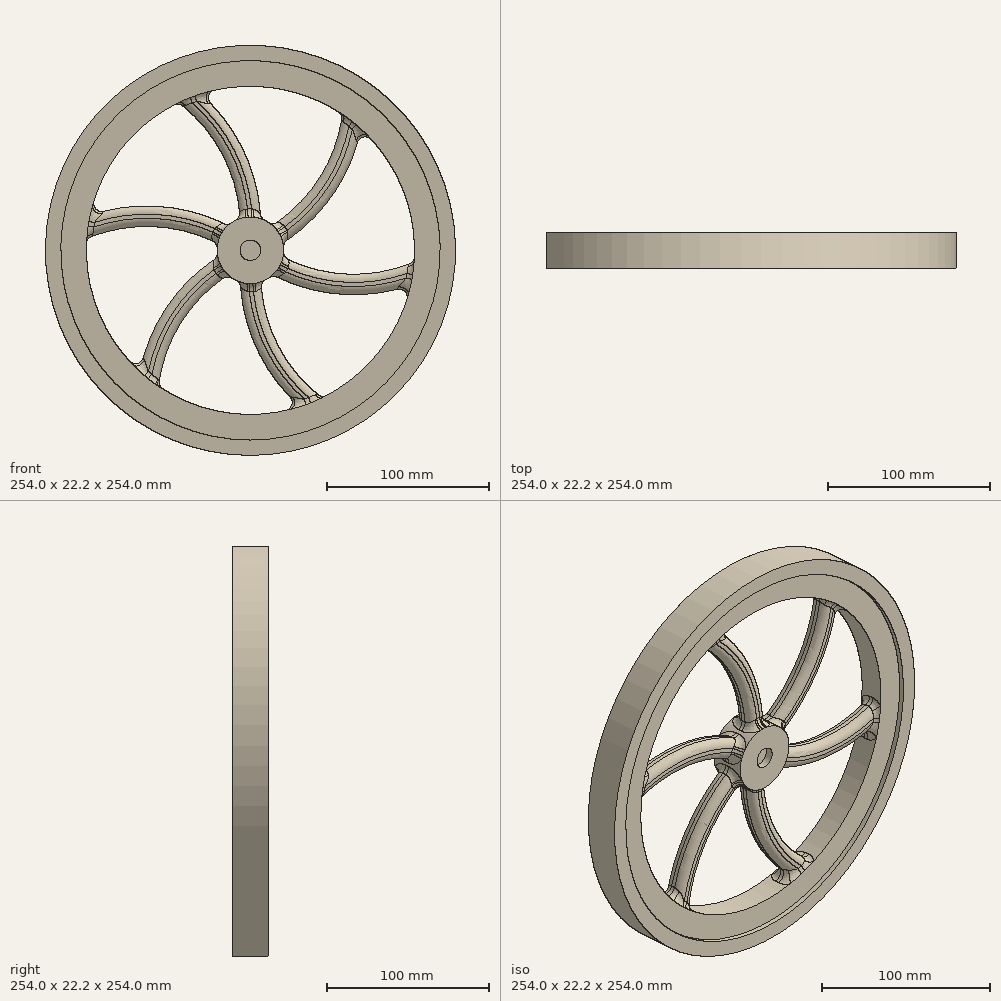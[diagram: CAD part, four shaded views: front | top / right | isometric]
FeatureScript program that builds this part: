
annotation { "Feature Type Name" : "Feature", "Feature Type Description" : "" }
export const myFeature = defineFeature(function(context is Context, id is Id, definition is map)
    precondition{}
    {
        {
            var Q0;
            Q0=qCreatedBy(makeId("Front.planeOp"),FACE);
            var sketch = newSketch(context, id + "F0", { "sketchPlane" : qUnion([Q0])});
            skCircle(sketch, "E0", {"center": v(0, 0) * mm, "radius": 127 * mm});
            skCircle(sketch, "E1", {"center": v(0, 0) * mm, "radius": 6.35 * mm});
            skCircle(sketch, "E2", {"center": v(0, 0) * mm, "radius": 101.6 * mm});
            skCircle(sketch, "E3", {"center": v(0, 0) * mm, "radius": 117.48 * mm});
            skCircle(sketch, "E4", {"center": v(0, 0) * mm, "radius": 20.64 * mm});
            skSolve(sketch);
        }
        {
            var Q0;
            Q0=makeQuery(id+"F0.imprint","IMPRINT",FACE,{"disambiguationData":[TD([[makeQuery(id+"F0.imprint","IMPRINT",EDGE,{"derivedFrom":sQuery(id+"F0.wireOp",EDGE,"E0")}),1.0]])]});
            extrude(context, id + "F1", {"entities" : qUnion([Q0]), "endBound" : BoundingType.SYMMETRIC, "depth" : 22.22 * mm, "offsetDistance" : 25.4 * mm});
        }
        {
            var Q0;
            Q0=makeQuery(id+"F0.imprint","IMPRINT",FACE,{"disambiguationData":[TD([[makeQuery(id+"F0.imprint","IMPRINT",EDGE,{"derivedFrom":sQuery(id+"F0.wireOp",EDGE,"E2")}),-1.0]])]});
            extrude(context, id + "F2", {"entities" : qUnion([Q0]), "operationType" : NewBodyOperationType.ADD, "endBound" : BoundingType.SYMMETRIC, "depth" : 15.88 * mm, "offsetDistance" : 25.4 * mm});
        }
        {
            var Q0;
            Q0=makeQuery(id+"F0.imprint","IMPRINT",FACE,{"disambiguationData":[TD([[makeQuery(id+"F0.imprint","IMPRINT",EDGE,{"derivedFrom":sQuery(id+"F0.wireOp",EDGE,"E1")}),-1.0]])]});
            extrude(context, id + "F3", {"entities" : qUnion([Q0]), "endBound" : BoundingType.SYMMETRIC, "depth" : 22.22 * mm, "offsetDistance" : 25.4 * mm});
        }
        {
            var Q0;
            Q0=makeQuery(id+"F0.imprint","IMPRINT",FACE,{"disambiguationData":[TD([[makeQuery(id+"F0.imprint","IMPRINT",EDGE,{"derivedFrom":sQuery(id+"F0.wireOp",EDGE,"E2")}),1.0]])]});
            var sketch = newSketch(context, id + "F4", { "sketchPlane" : qUnion([Q0])});
            skLineSegment(sketch, "E5", {"start": v(0, 0) * mm, "end": v(0, 137.05) * mm, "construction": true});
            skArc(sketch, "E6", {"start": v(0, 14.86) * mm, "mid": v(-11.63, 62.26) * mm, "end": v(-43.88, 98.88) * mm});
            skArc(sketch, "E7.0.startCap", {"start": v(6.35, 14.86) * mm, "mid": v(0, 8.51) * mm, "end": v(-6.35, 14.86) * mm});
            skArc(sketch, "E7.0.endCap", {"start": v(-47.5, 93.67) * mm, "mid": v(-49.09, 102.51) * mm, "end": v(-40.25, 104.1) * mm});
            skArc(sketch, "E7.0.left", {"start": v(-6.35, 14.86) * mm, "mid": v(-17.26, 59.32) * mm, "end": v(-47.5, 93.67) * mm});
            skArc(sketch, "E7.0.right", {"start": v(6.35, 14.86) * mm, "mid": v(-6, 65.2) * mm, "end": v(-40.25, 104.1) * mm});
            skArc(sketch, "E8.1.0", {"start": v(-9.7, 12.93) * mm, "mid": v(-59.46, 27.4) * mm, "end": v(-110.27, 17.19) * mm});
            skArc(sketch, "E8.1.1", {"start": v(-104.88, 5.7) * mm, "mid": v(-113.32, 8.74) * mm, "end": v(-110.27, 17.19) * mm});
            skArc(sketch, "E8.1.2", {"start": v(-16.04, 1.93) * mm, "mid": v(-60, 14.71) * mm, "end": v(-104.88, 5.7) * mm});
            skArc(sketch, "E8.1.3", {"start": v(-9.7, 12.93) * mm, "mid": v(-7.37, 4.26) * mm, "end": v(-16.04, 1.93) * mm});
            skArc(sketch, "E8.2.0", {"start": v(-16.04, -1.93) * mm, "mid": v(-53.46, -37.8) * mm, "end": v(-70.02, -86.9) * mm});
            skArc(sketch, "E8.2.1", {"start": v(-57.37, -87.98) * mm, "mid": v(-64.23, -93.77) * mm, "end": v(-70.02, -86.9) * mm});
            skArc(sketch, "E8.2.2", {"start": v(-9.7, -12.93) * mm, "mid": v(-42.74, -44.6) * mm, "end": v(-57.37, -87.98) * mm});
            skArc(sketch, "E8.2.3", {"start": v(-16.04, -1.93) * mm, "mid": v(-7.37, -4.26) * mm, "end": v(-9.7, -12.93) * mm});
            skArc(sketch, "E8.3.0", {"start": v(-6.35, -14.86) * mm, "mid": v(6, -65.2) * mm, "end": v(40.25, -104.1) * mm});
            skArc(sketch, "E8.3.1", {"start": v(47.5, -93.67) * mm, "mid": v(49.09, -102.51) * mm, "end": v(40.25, -104.1) * mm});
            skArc(sketch, "E8.3.2", {"start": v(6.35, -14.86) * mm, "mid": v(17.26, -59.32) * mm, "end": v(47.5, -93.67) * mm});
            skArc(sketch, "E8.3.3", {"start": v(-6.35, -14.86) * mm, "mid": v(0, -8.51) * mm, "end": v(6.35, -14.86) * mm});
            skArc(sketch, "E8.4.0", {"start": v(9.7, -12.93) * mm, "mid": v(59.46, -27.4) * mm, "end": v(110.27, -17.19) * mm});
            skArc(sketch, "E8.4.1", {"start": v(104.88, -5.7) * mm, "mid": v(113.32, -8.74) * mm, "end": v(110.27, -17.19) * mm});
            skArc(sketch, "E8.4.2", {"start": v(16.04, -1.93) * mm, "mid": v(60, -14.71) * mm, "end": v(104.88, -5.7) * mm});
            skArc(sketch, "E8.4.3", {"start": v(9.7, -12.93) * mm, "mid": v(7.37, -4.26) * mm, "end": v(16.04, -1.93) * mm});
            skArc(sketch, "E8.5.0", {"start": v(16.04, 1.93) * mm, "mid": v(53.46, 37.8) * mm, "end": v(70.02, 86.9) * mm});
            skArc(sketch, "E8.5.1", {"start": v(57.37, 87.98) * mm, "mid": v(64.23, 93.77) * mm, "end": v(70.02, 86.9) * mm});
            skArc(sketch, "E8.5.2", {"start": v(9.7, 12.93) * mm, "mid": v(42.74, 44.6) * mm, "end": v(57.37, 87.98) * mm});
            skArc(sketch, "E8.5.3", {"start": v(16.04, 1.93) * mm, "mid": v(7.37, 4.26) * mm, "end": v(9.7, 12.93) * mm});
            skPoint(sketch, "E8.center", {"position": v(0, 0) * mm});
            skSolve(sketch);
        }
        {
            var Q0;
            {var subQ0=sQuery(id+"F4.wireOp",EDGE,"E6");var subQ1=makeQuery(id+"F0.imprint","IMPRINT",EDGE,{"derivedFrom":sQuery(id+"F0.wireOp",EDGE,"E2")});var subQ2=makeQuery(id+"F4.imprint","INTERSECT",VERTEX,{"derivedFrom":[subQ1,subQ0]});Q0=makeQuery(id+"F4.imprint","IMPRINT",FACE,{"disambiguationData":[TD([[makeQuery(id+"F4.imprint","IMPRINT",EDGE,{"disambiguationData":[TD([[subQ2,1.0]])],"derivedFrom":subQ0}),1.0]])]});}
            var Q1;
            {var subQ0=sQuery(id+"F4.wireOp",EDGE,"E8.3.1");Q1=makeQuery(id+"F4.imprint","IMPRINT",FACE,{"disambiguationData":[TD([[makeQuery(id+"F4.imprint","IMPRINT",EDGE,{"derivedFrom":subQ0}),-1.0]])]});}
            var Q2;
            {var subQ4=sQuery(id+"F4.wireOp",EDGE,"E7.0.startCap");Q2=makeQuery(id+"F4.imprint","IMPRINT",FACE,{"disambiguationData":[TD([[makeQuery(id+"F4.imprint","IMPRINT",EDGE,{"derivedFrom":subQ4}),-1.0]])]});}
            var Q3;
            {var subQ0=sQuery(id+"F4.wireOp",EDGE,"E8.2.3");Q3=makeQuery(id+"F4.imprint","IMPRINT",FACE,{"disambiguationData":[TD([[makeQuery(id+"F4.imprint","IMPRINT",EDGE,{"derivedFrom":subQ0}),-1.0]])]});}
            var Q4;
            {var subQ0=sQuery(id+"F4.wireOp",EDGE,"E8.5.0");var subQ1=makeQuery(id+"F0.imprint","IMPRINT",EDGE,{"derivedFrom":sQuery(id+"F0.wireOp",EDGE,"E2")});var subQ2=makeQuery(id+"F4.imprint","INTERSECT",VERTEX,{"derivedFrom":[subQ1,subQ0]});Q4=makeQuery(id+"F4.imprint","IMPRINT",FACE,{"disambiguationData":[TD([[makeQuery(id+"F4.imprint","IMPRINT",EDGE,{"disambiguationData":[TD([[subQ2,1.0]])],"derivedFrom":subQ0}),1.0]])]});}
            var Q5;
            {var subQ0=sQuery(id+"F4.wireOp",EDGE,"E6");var subQ1=makeQuery(id+"F0.imprint","IMPRINT",EDGE,{"derivedFrom":sQuery(id+"F0.wireOp",EDGE,"E2")});var subQ2=makeQuery(id+"F4.imprint","INTERSECT",VERTEX,{"derivedFrom":[subQ1,subQ0]});Q5=makeQuery(id+"F4.imprint","IMPRINT",FACE,{"disambiguationData":[TD([[makeQuery(id+"F4.imprint","IMPRINT",EDGE,{"disambiguationData":[TD([[subQ2,1.0]])],"derivedFrom":subQ0}),-1.0]])]});}
            var Q6;
            {var subQ0=sQuery(id+"F4.wireOp",EDGE,"E8.4.1");Q6=makeQuery(id+"F4.imprint","IMPRINT",FACE,{"disambiguationData":[TD([[makeQuery(id+"F4.imprint","IMPRINT",EDGE,{"derivedFrom":subQ0}),-1.0]])]});}
            var Q7;
            {var subQ0=sQuery(id+"F4.wireOp",EDGE,"E8.5.1");Q7=makeQuery(id+"F4.imprint","IMPRINT",FACE,{"disambiguationData":[TD([[makeQuery(id+"F4.imprint","IMPRINT",EDGE,{"derivedFrom":subQ0}),-1.0]])]});}
            var Q8;
            {var subQ0=sQuery(id+"F4.wireOp",EDGE,"E8.5.3");Q8=makeQuery(id+"F4.imprint","IMPRINT",FACE,{"disambiguationData":[TD([[makeQuery(id+"F4.imprint","IMPRINT",EDGE,{"derivedFrom":subQ0}),-1.0]])]});}
            var Q9;
            {var subQ0=sQuery(id+"F4.wireOp",EDGE,"E8.1.1");Q9=makeQuery(id+"F4.imprint","IMPRINT",FACE,{"disambiguationData":[TD([[makeQuery(id+"F4.imprint","IMPRINT",EDGE,{"derivedFrom":subQ0}),-1.0]])]});}
            var Q10;
            {var subQ0=sQuery(id+"F4.wireOp",EDGE,"E8.2.1");Q10=makeQuery(id+"F4.imprint","IMPRINT",FACE,{"disambiguationData":[TD([[makeQuery(id+"F4.imprint","IMPRINT",EDGE,{"derivedFrom":subQ0}),-1.0]])]});}
            var Q11;
            {var subQ0=sQuery(id+"F4.wireOp",EDGE,"E8.2.0");var subQ1=makeQuery(id+"F0.imprint","IMPRINT",EDGE,{"derivedFrom":sQuery(id+"F0.wireOp",EDGE,"E2")});var subQ2=makeQuery(id+"F4.imprint","INTERSECT",VERTEX,{"derivedFrom":[subQ1,subQ0]});Q11=makeQuery(id+"F4.imprint","IMPRINT",FACE,{"disambiguationData":[TD([[makeQuery(id+"F4.imprint","IMPRINT",EDGE,{"disambiguationData":[TD([[subQ2,1.0]])],"derivedFrom":subQ0}),1.0]])]});}
            var Q12;
            {var subQ0=sQuery(id+"F4.wireOp",EDGE,"E8.3.0");var subQ1=makeQuery(id+"F0.imprint","IMPRINT",EDGE,{"derivedFrom":sQuery(id+"F0.wireOp",EDGE,"E2")});var subQ2=makeQuery(id+"F4.imprint","INTERSECT",VERTEX,{"derivedFrom":[subQ1,subQ0]});Q12=makeQuery(id+"F4.imprint","IMPRINT",FACE,{"disambiguationData":[TD([[makeQuery(id+"F4.imprint","IMPRINT",EDGE,{"disambiguationData":[TD([[subQ2,1.0]])],"derivedFrom":subQ0}),1.0]])]});}
            var Q13;
            {var subQ0=sQuery(id+"F4.wireOp",EDGE,"E8.3.3");Q13=makeQuery(id+"F4.imprint","IMPRINT",FACE,{"disambiguationData":[TD([[makeQuery(id+"F4.imprint","IMPRINT",EDGE,{"derivedFrom":subQ0}),-1.0]])]});}
            var Q14;
            {var subQ0=sQuery(id+"F4.wireOp",EDGE,"E8.4.0");var subQ1=makeQuery(id+"F0.imprint","IMPRINT",EDGE,{"derivedFrom":sQuery(id+"F0.wireOp",EDGE,"E2")});var subQ2=makeQuery(id+"F4.imprint","INTERSECT",VERTEX,{"derivedFrom":[subQ1,subQ0]});Q14=makeQuery(id+"F4.imprint","IMPRINT",FACE,{"disambiguationData":[TD([[makeQuery(id+"F4.imprint","IMPRINT",EDGE,{"disambiguationData":[TD([[subQ2,1.0]])],"derivedFrom":subQ0}),1.0]])]});}
            var Q15;
            {var subQ0=sQuery(id+"F4.wireOp",EDGE,"E8.1.3");Q15=makeQuery(id+"F4.imprint","IMPRINT",FACE,{"disambiguationData":[TD([[makeQuery(id+"F4.imprint","IMPRINT",EDGE,{"derivedFrom":subQ0}),-1.0]])]});}
            var Q16;
            {var subQ0=sQuery(id+"F4.wireOp",EDGE,"E8.4.3");Q16=makeQuery(id+"F4.imprint","IMPRINT",FACE,{"disambiguationData":[TD([[makeQuery(id+"F4.imprint","IMPRINT",EDGE,{"derivedFrom":subQ0}),-1.0]])]});}
            var Q17;
            {var subQ1=sQuery(id+"F4.wireOp",EDGE,"E7.0.endCap");Q17=makeQuery(id+"F4.imprint","IMPRINT",FACE,{"disambiguationData":[TD([[makeQuery(id+"F4.imprint","IMPRINT",EDGE,{"derivedFrom":subQ1}),-1.0]])]});}
            var Q18;
            {var subQ0=sQuery(id+"F4.wireOp",EDGE,"E8.1.0");var subQ1=makeQuery(id+"F0.imprint","IMPRINT",EDGE,{"derivedFrom":sQuery(id+"F0.wireOp",EDGE,"E2")});var subQ2=makeQuery(id+"F4.imprint","INTERSECT",VERTEX,{"derivedFrom":[subQ1,subQ0]});Q18=makeQuery(id+"F4.imprint","IMPRINT",FACE,{"disambiguationData":[TD([[makeQuery(id+"F4.imprint","IMPRINT",EDGE,{"disambiguationData":[TD([[subQ2,1.0]])],"derivedFrom":subQ0}),1.0]])]});}
            extrude(context, id + "F5", {"entities" : qUnion([Q0, Q1, Q2, Q3, Q4, Q5, Q6, Q7, Q8, Q9, Q10, Q11, Q12, Q13, Q14, Q15, Q16, Q17, Q18]), "operationType" : NewBodyOperationType.ADD, "endBound" : BoundingType.SYMMETRIC, "depth" : 12.7 * mm, "offsetDistance" : 25.4 * mm});
        }
        {
            var Q0;
            Q0=makeQuery(id+"F5.opExtrude","CAP_EDGE",EDGE,{"disambiguationData":[OSD([sQuery(id+"F4.wireOp",EDGE,"E7.0.left")])],"isStart":false});
            var Q1;
            Q1=makeQuery(id+"F5.opExtrude","CAP_EDGE",EDGE,{"disambiguationData":[OSD([sQuery(id+"F4.wireOp",EDGE,"E7.0.right")])],"isStart":false});
            var Q2;
            Q2=makeQuery(id+"F5.opExtrude","CAP_EDGE",EDGE,{"disambiguationData":[OSD([sQuery(id+"F4.wireOp",EDGE,"E8.1.0")])],"isStart":false});
            var Q3;
            Q3=makeQuery(id+"F5.opExtrude","CAP_EDGE",EDGE,{"disambiguationData":[OSD([sQuery(id+"F4.wireOp",EDGE,"E8.1.2")])],"isStart":false});
            var Q4;
            Q4=makeQuery(id+"F5.opExtrude","CAP_EDGE",EDGE,{"disambiguationData":[OSD([sQuery(id+"F4.wireOp",EDGE,"E8.2.0")])],"isStart":false});
            var Q5;
            Q5=makeQuery(id+"F5.opExtrude","CAP_EDGE",EDGE,{"disambiguationData":[OSD([sQuery(id+"F4.wireOp",EDGE,"E8.2.2")])],"isStart":false});
            var Q6;
            Q6=makeQuery(id+"F5.opExtrude","CAP_EDGE",EDGE,{"disambiguationData":[OSD([sQuery(id+"F4.wireOp",EDGE,"E8.3.0")])],"isStart":false});
            var Q7;
            Q7=makeQuery(id+"F5.opExtrude","CAP_EDGE",EDGE,{"disambiguationData":[OSD([sQuery(id+"F4.wireOp",EDGE,"E8.3.2")])],"isStart":false});
            var Q8;
            Q8=makeQuery(id+"F5.opExtrude","CAP_EDGE",EDGE,{"disambiguationData":[OSD([sQuery(id+"F4.wireOp",EDGE,"E8.4.0")])],"isStart":false});
            var Q9;
            Q9=makeQuery(id+"F5.opExtrude","CAP_EDGE",EDGE,{"disambiguationData":[OSD([sQuery(id+"F4.wireOp",EDGE,"E8.4.2")])],"isStart":false});
            var Q10;
            Q10=makeQuery(id+"F5.opExtrude","CAP_EDGE",EDGE,{"disambiguationData":[OSD([sQuery(id+"F4.wireOp",EDGE,"E8.5.0")])],"isStart":false});
            var Q11;
            Q11=makeQuery(id+"F5.opExtrude","CAP_EDGE",EDGE,{"disambiguationData":[OSD([sQuery(id+"F4.wireOp",EDGE,"E8.5.2")])],"isStart":false});
            fillet(context, id + "F6", {"entities" : qUnion([Q0, Q1, Q2, Q3, Q4, Q5, Q6, Q7, Q8, Q9, Q10, Q11]), "radius" : 5.08 * mm, "tangentPropagation" : true, "allowEdgeOverflow" : false});
        }
        {
            var Q0;
            Q0=makeQuery(id+"F5.opExtrude","CAP_EDGE",EDGE,{"disambiguationData":[OSD([sQuery(id+"F4.wireOp",EDGE,"E7.0.left")])],"isStart":true});
            var Q1;
            Q1=makeQuery(id+"F5.opExtrude","CAP_EDGE",EDGE,{"disambiguationData":[OSD([sQuery(id+"F4.wireOp",EDGE,"E7.0.right")])],"isStart":true});
            var Q2;
            Q2=makeQuery(id+"F5.opExtrude","CAP_EDGE",EDGE,{"disambiguationData":[OSD([sQuery(id+"F4.wireOp",EDGE,"E8.5.2")])],"isStart":true});
            var Q3;
            Q3=makeQuery(id+"F5.opExtrude","CAP_EDGE",EDGE,{"disambiguationData":[OSD([sQuery(id+"F4.wireOp",EDGE,"E8.5.0")])],"isStart":true});
            var Q4;
            Q4=makeQuery(id+"F5.opExtrude","CAP_EDGE",EDGE,{"disambiguationData":[OSD([sQuery(id+"F4.wireOp",EDGE,"E8.4.2")])],"isStart":true});
            var Q5;
            Q5=makeQuery(id+"F5.opExtrude","CAP_EDGE",EDGE,{"disambiguationData":[OSD([sQuery(id+"F4.wireOp",EDGE,"E8.4.0")])],"isStart":true});
            var Q6;
            Q6=makeQuery(id+"F5.opExtrude","CAP_EDGE",EDGE,{"disambiguationData":[OSD([sQuery(id+"F4.wireOp",EDGE,"E8.3.2")])],"isStart":true});
            var Q7;
            Q7=makeQuery(id+"F5.opExtrude","CAP_EDGE",EDGE,{"disambiguationData":[OSD([sQuery(id+"F4.wireOp",EDGE,"E8.3.0")])],"isStart":true});
            var Q8;
            Q8=makeQuery(id+"F5.opExtrude","CAP_EDGE",EDGE,{"disambiguationData":[OSD([sQuery(id+"F4.wireOp",EDGE,"E8.2.2")])],"isStart":true});
            var Q9;
            Q9=makeQuery(id+"F5.opExtrude","CAP_EDGE",EDGE,{"disambiguationData":[OSD([sQuery(id+"F4.wireOp",EDGE,"E8.2.0")])],"isStart":true});
            var Q10;
            Q10=makeQuery(id+"F5.opExtrude","CAP_EDGE",EDGE,{"disambiguationData":[OSD([sQuery(id+"F4.wireOp",EDGE,"E8.1.2")])],"isStart":true});
            var Q11;
            Q11=makeQuery(id+"F5.opExtrude","CAP_EDGE",EDGE,{"disambiguationData":[OSD([sQuery(id+"F4.wireOp",EDGE,"E8.1.0")])],"isStart":true});
            fillet(context, id + "F7", {"entities" : qUnion([Q0, Q1, Q2, Q3, Q4, Q5, Q6, Q7, Q8, Q9, Q10, Q11]), "radius" : 5.08 * mm, "tangentPropagation" : true, "allowEdgeOverflow" : false});
        }
        {
            var Q0;
            Q0=makeQuery(id+"F7.opFillet","BLEND_EDGE",EDGE,{"blendedFrom":[makeQuery(id+"F5.opExtrude","CAP_EDGE",EDGE,{"disambiguationData":[OSD([sQuery(id+"F4.wireOp",EDGE,"E8.4.2")])],"isStart":true}),makeQuery(id+"F2.opExtrude","SWEPT_FACE",FACE,{"disambiguationData":[OSD([sQuery(id+"F0.wireOp",EDGE,"E2")])]})],"blendedInto":[makeQuery(id+"F2.opExtrude","SWEPT_FACE",FACE,{"disambiguationData":[OSD([sQuery(id+"F0.wireOp",EDGE,"E2")])]})]});
            var Q1;
            Q1=makeQuery(id+"F6.opFillet","BLEND_EDGE",EDGE,{"blendedFrom":[makeQuery(id+"F5.opExtrude","CAP_EDGE",EDGE,{"disambiguationData":[OSD([sQuery(id+"F4.wireOp",EDGE,"E8.3.2")])],"isStart":false}),makeQuery(id+"F2.opExtrude","SWEPT_FACE",FACE,{"disambiguationData":[OSD([sQuery(id+"F0.wireOp",EDGE,"E2")])]})],"blendedInto":[makeQuery(id+"F2.opExtrude","SWEPT_FACE",FACE,{"disambiguationData":[OSD([sQuery(id+"F0.wireOp",EDGE,"E2")])]})]});
            var Q2;
            Q2=makeQuery(id+"F6.opFillet","BLEND_EDGE",EDGE,{"blendedFrom":[makeQuery(id+"F5.opExtrude","CAP_EDGE",EDGE,{"disambiguationData":[OSD([sQuery(id+"F4.wireOp",EDGE,"E8.2.2")])],"isStart":false}),makeQuery(id+"F2.opExtrude","SWEPT_FACE",FACE,{"disambiguationData":[OSD([sQuery(id+"F0.wireOp",EDGE,"E2")])]})],"blendedInto":[makeQuery(id+"F2.opExtrude","SWEPT_FACE",FACE,{"disambiguationData":[OSD([sQuery(id+"F0.wireOp",EDGE,"E2")])]})]});
            var Q3;
            Q3=makeQuery(id+"F6.opFillet","BLEND_EDGE",EDGE,{"blendedFrom":[makeQuery(id+"F5.opExtrude","CAP_EDGE",EDGE,{"disambiguationData":[OSD([sQuery(id+"F4.wireOp",EDGE,"E8.1.2")])],"isStart":false}),makeQuery(id+"F2.opExtrude","SWEPT_FACE",FACE,{"disambiguationData":[OSD([sQuery(id+"F0.wireOp",EDGE,"E2")])]})],"blendedInto":[makeQuery(id+"F2.opExtrude","SWEPT_FACE",FACE,{"disambiguationData":[OSD([sQuery(id+"F0.wireOp",EDGE,"E2")])]})]});
            var Q4;
            Q4=makeQuery(id+"F7.opFillet","BLEND_EDGE",EDGE,{"blendedFrom":[makeQuery(id+"F5.opExtrude","CAP_EDGE",EDGE,{"disambiguationData":[OSD([sQuery(id+"F4.wireOp",EDGE,"E7.0.left")])],"isStart":true}),makeQuery(id+"F2.opExtrude","SWEPT_FACE",FACE,{"disambiguationData":[OSD([sQuery(id+"F0.wireOp",EDGE,"E2")])]})],"blendedInto":[makeQuery(id+"F2.opExtrude","SWEPT_FACE",FACE,{"disambiguationData":[OSD([sQuery(id+"F0.wireOp",EDGE,"E2")])]})]});
            var Q5;
            Q5=makeQuery(id+"F7.opFillet","BLEND_EDGE",EDGE,{"blendedFrom":[makeQuery(id+"F5.opExtrude","CAP_EDGE",EDGE,{"disambiguationData":[OSD([sQuery(id+"F4.wireOp",EDGE,"E8.5.0")])],"isStart":true}),makeQuery(id+"F2.opExtrude","SWEPT_FACE",FACE,{"disambiguationData":[OSD([sQuery(id+"F0.wireOp",EDGE,"E2")])]})],"blendedInto":[makeQuery(id+"F2.opExtrude","SWEPT_FACE",FACE,{"disambiguationData":[OSD([sQuery(id+"F0.wireOp",EDGE,"E2")])]})]});
            fillet(context, id + "F8", {"entities" : qUnion([Q0, Q1, Q2, Q3, Q4, Q5]), "radius" : 5.08 * mm, "tangentPropagation" : true, "allowEdgeOverflow" : false});
        }
        {
            var Q0;
            Q0=makeQuery(id+"F6.opFillet","BLEND_EDGE",EDGE,{"blendedFrom":[makeQuery(id+"F5.opExtrude","CAP_EDGE",EDGE,{"disambiguationData":[OSD([sQuery(id+"F4.wireOp",EDGE,"E7.0.right")])],"isStart":false}),makeQuery(id+"F3.opExtrude","SWEPT_FACE",FACE,{"disambiguationData":[OSD([sQuery(id+"F0.wireOp",EDGE,"E4")])]})],"blendedInto":[makeQuery(id+"F3.opExtrude","SWEPT_FACE",FACE,{"disambiguationData":[OSD([sQuery(id+"F0.wireOp",EDGE,"E4")])]})]});
            var Q1;
            Q1=makeQuery(id+"F6.opFillet","BLEND_EDGE",EDGE,{"blendedFrom":[makeQuery(id+"F5.opExtrude","CAP_EDGE",EDGE,{"disambiguationData":[OSD([sQuery(id+"F4.wireOp",EDGE,"E8.1.0")])],"isStart":false}),makeQuery(id+"F3.opExtrude","SWEPT_FACE",FACE,{"disambiguationData":[OSD([sQuery(id+"F0.wireOp",EDGE,"E4")])]})],"blendedInto":[makeQuery(id+"F3.opExtrude","SWEPT_FACE",FACE,{"disambiguationData":[OSD([sQuery(id+"F0.wireOp",EDGE,"E4")])]})]});
            var Q2;
            Q2=makeQuery(id+"F6.opFillet","BLEND_EDGE",EDGE,{"blendedFrom":[makeQuery(id+"F5.opExtrude","CAP_EDGE",EDGE,{"disambiguationData":[OSD([sQuery(id+"F4.wireOp",EDGE,"E8.2.0")])],"isStart":false}),makeQuery(id+"F3.opExtrude","SWEPT_FACE",FACE,{"disambiguationData":[OSD([sQuery(id+"F0.wireOp",EDGE,"E4")])]})],"blendedInto":[makeQuery(id+"F3.opExtrude","SWEPT_FACE",FACE,{"disambiguationData":[OSD([sQuery(id+"F0.wireOp",EDGE,"E4")])]})]});
            var Q3;
            Q3=makeQuery(id+"F6.opFillet","BLEND_EDGE",EDGE,{"blendedFrom":[makeQuery(id+"F5.opExtrude","CAP_EDGE",EDGE,{"disambiguationData":[OSD([sQuery(id+"F4.wireOp",EDGE,"E8.3.0")])],"isStart":false}),makeQuery(id+"F3.opExtrude","SWEPT_FACE",FACE,{"disambiguationData":[OSD([sQuery(id+"F0.wireOp",EDGE,"E4")])]})],"blendedInto":[makeQuery(id+"F3.opExtrude","SWEPT_FACE",FACE,{"disambiguationData":[OSD([sQuery(id+"F0.wireOp",EDGE,"E4")])]})]});
            var Q4;
            Q4=makeQuery(id+"F6.opFillet","BLEND_EDGE",EDGE,{"blendedFrom":[makeQuery(id+"F5.opExtrude","CAP_EDGE",EDGE,{"disambiguationData":[OSD([sQuery(id+"F4.wireOp",EDGE,"E8.4.0")])],"isStart":false}),makeQuery(id+"F3.opExtrude","SWEPT_FACE",FACE,{"disambiguationData":[OSD([sQuery(id+"F0.wireOp",EDGE,"E4")])]})],"blendedInto":[makeQuery(id+"F3.opExtrude","SWEPT_FACE",FACE,{"disambiguationData":[OSD([sQuery(id+"F0.wireOp",EDGE,"E4")])]})]});
            var Q5;
            Q5=makeQuery(id+"F6.opFillet","BLEND_EDGE",EDGE,{"blendedFrom":[makeQuery(id+"F5.opExtrude","CAP_EDGE",EDGE,{"disambiguationData":[OSD([sQuery(id+"F4.wireOp",EDGE,"E8.5.2")])],"isStart":false}),makeQuery(id+"F3.opExtrude","SWEPT_FACE",FACE,{"disambiguationData":[OSD([sQuery(id+"F0.wireOp",EDGE,"E4")])]})],"blendedInto":[makeQuery(id+"F3.opExtrude","SWEPT_FACE",FACE,{"disambiguationData":[OSD([sQuery(id+"F0.wireOp",EDGE,"E4")])]})]});
            fillet(context, id + "F9", {"entities" : qUnion([Q0, Q1, Q2, Q3, Q4, Q5]), "radius" : 5.08 * mm, "tangentPropagation" : true, "allowEdgeOverflow" : false});
        }
    });
